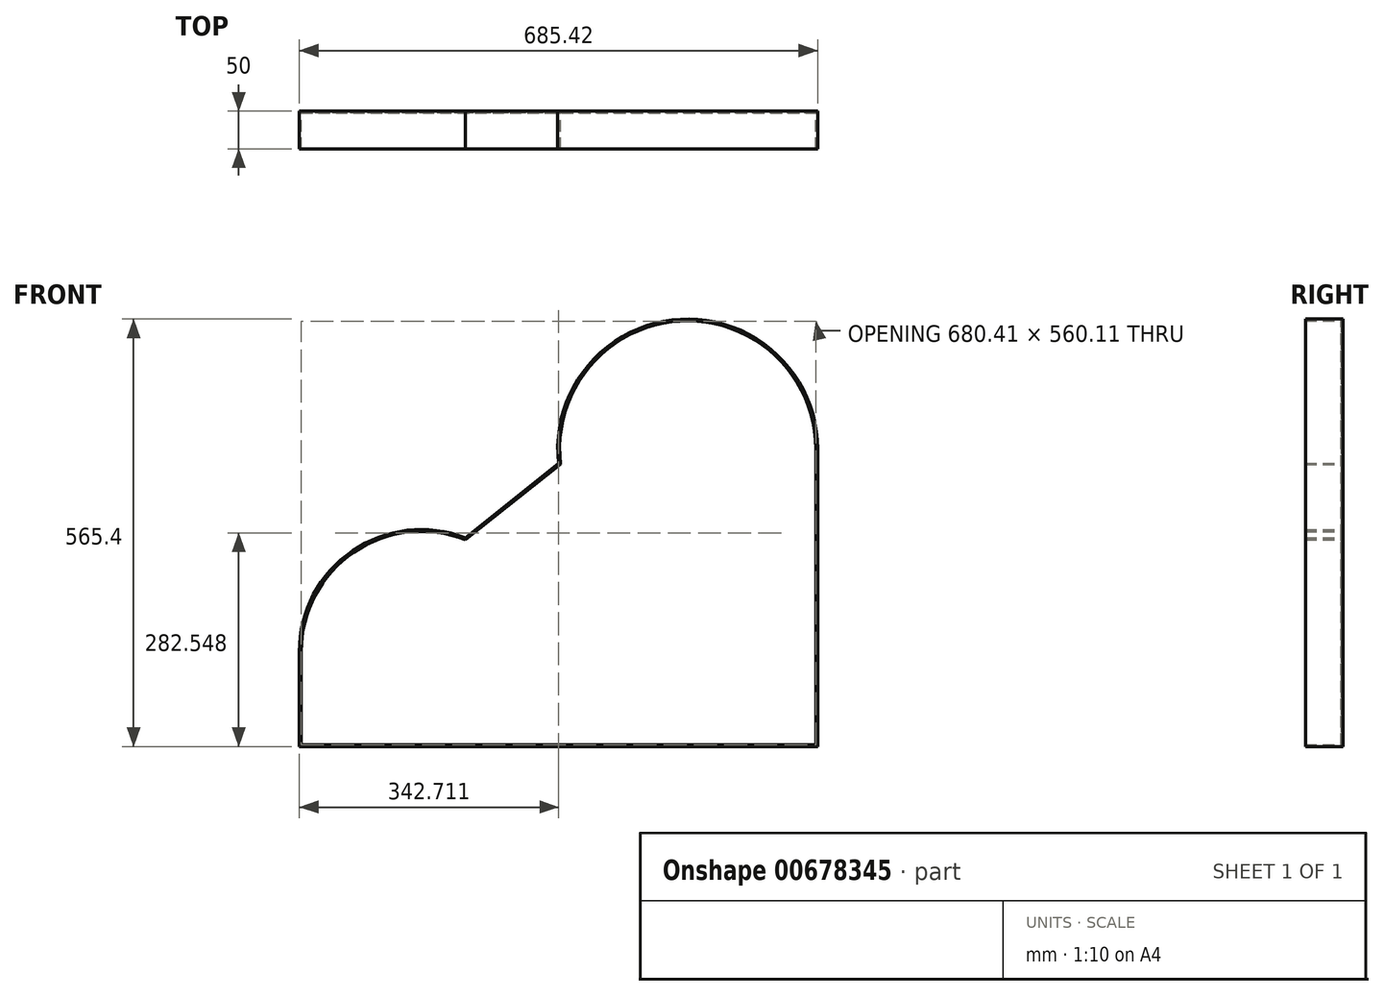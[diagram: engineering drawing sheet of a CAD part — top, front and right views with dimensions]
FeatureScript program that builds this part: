
annotation { "Feature Type Name" : "Feature", "Feature Type Description" : "" }
export const myFeature = defineFeature(function(context is Context, id is Id, definition is map)
    precondition{}
    {
        {
            var Q0;
            Q0=qCreatedBy(makeId("Front.planeOp"),FACE);
            var sketch = newSketch(context, id + "F0", { "sketchPlane" : qUnion([Q0])});
            skLineSegment(sketch, "E0", {"start": v(-64.19, 12.95) * mm, "end": v(-64.19, -112.67) * mm});
            skLineSegment(sketch, "E1", {"start": v(-64.19, -112.67) * mm, "end": v(621.23, -112.67) * mm});
            skLineSegment(sketch, "E2", {"start": v(621.23, -112.67) * mm, "end": v(621.23, 280.9) * mm});
            skArc(sketch, "E3", {"start": v(621.23, 280.9) * mm, "mid": v(439.87, 452.47) * mm, "end": v(278.62, 261.88) * mm});
            skLineSegment(sketch, "E4", {"start": v(278.62, 261.88) * mm, "end": v(155.26, 163.5) * mm});
            skArc(sketch, "E5", {"start": v(-64.19, 12.95) * mm, "mid": v(5.9, 146) * mm, "end": v(155.26, 163.5) * mm});
            skSolve(sketch);
        }
        {
            var Q0;
            Q0=makeQuery(id+"F0.imprint","IMPRINT",FACE,{"disambiguationData":[TD([[makeQuery(id+"F0.imprint","IMPRINT",EDGE,{"derivedFrom":sQuery(id+"F0.wireOp",EDGE,"E0")}),1.0]])]});
            extrude(context, id + "F1", {"entities" : qUnion([Q0]), "depth" : 50 * mm, "offsetDistance" : 25 * mm});
        }
        {
            var Q0;
            Q0=makeQuery(id+"F1.opExtrude","CAP_FACE",FACE,{"disambiguationData":[OSD([sQuery(id+"F0.wireOp",EDGE,"E0"),sQuery(id+"F0.wireOp",EDGE,"E1"),sQuery(id+"F0.wireOp",EDGE,"E2"),sQuery(id+"F0.wireOp",EDGE,"E3"),sQuery(id+"F0.wireOp",EDGE,"E4"),sQuery(id+"F0.wireOp",EDGE,"E5")])],"isStart":false});
            shell(context, id + "F2", {"entities" : qUnion([Q0]), "thickness" : 2.5 * mm});
        }
    });
